FCSTD DOCUMENT  (FreeCAD 0.19R21897 (Git))
Label: MASTER2
License: cc-by-sa
LicenseURL: http://creativecommons.org/licenses/by-sa/4.0/
objects: Sketcher::SketchObject×2, PartDesign::Line×1, PartDesign::Plane×1, PartDesign::Body×1
note: 5 computed .brp shape members not serialized (recipe doc carries the construction recipe); baked Part::Feature solids carry a one-line shape summary decoded from their .brp

FEATURE [Sketcher::SketchObject] Sketch  label="MASTER"
  MapMode = 5
  Placement = pos=(0,0,0) rot=(0.57735,0.57735,0.57735;2.0944rad)
  Support = -> [YZ_Plane]
  sketch-geometry (3):
    g0: Circle CenterX=0 CenterY=1066.8 CenterZ=0 NormalX=0 NormalY=0 NormalZ=1 AngleXU=0 Radius=10
    g1: LineSegment StartX=-609.6 StartY=0 StartZ=0 EndX=304.8 EndY=0 EndZ=0
    g2: LineSegment StartX=0 StartY=1066.8 StartZ=0 EndX=0 EndY=0 EndZ=0
  constraints (9):
    c: PointOnObject(g1,g-1)
    c: PointOnObject(g1,g-1)
    c: Coincident(g2,g0)
    c: Vertical(g2)
    c: DistanceY(g0) = 1066.8
    c: DistanceX(g1,g1) = 914.4
    c: Coincident(g2,g-1)
    c: DistanceX(g2,g1) = 304.8
    c: Radius(g0) = 10
FEATURE [PartDesign::Line] DatumLine  label="RollerAxis"
  AttacherType = Attacher::AttachEngineLine
  Length = 20
  MapMode = 19
  Placement = pos=(-2.369e-13,2.363e-13,1066.8) rot=(0.57735,0.57735,0.57735;2.0944rad)
  ResizeMode = 0
  Support = -> [Sketch]
FEATURE [PartDesign::Plane] DatumPlane  label="HorizontalPlane"
  Length = 355.483
  MapMode = 49
  Placement = pos=(6.77e-14,304.8,-6.77e-14) rot=(0,0,-1;1.5708rad)
  ResizeMode = 0
  Support = -> [Sketch]
  Width = 75.6827
FEATURE [Sketcher::SketchObject] Sketch001  label="HorizontalMaster"
  ExternalGeometry = -> [Sketch]
  MapMode = 5
  Placement = pos=(6.77e-14,304.8,-6.77e-14) rot=(0,0,-1;1.5708rad)
  Support = -> [DatumPlane]
  sketch-geometry (4):
    g0: LineSegment StartX=304.8 StartY=1079.5 StartZ=0 EndX=304.8 EndY=-1079.5 EndZ=0
    g1: LineSegment StartX=0 StartY=1079.5 StartZ=0 EndX=914.4 EndY=1079.5 EndZ=0
    g2: LineSegment StartX=0 StartY=-1079.5 StartZ=0 EndX=914.4 EndY=-1079.5 EndZ=0
    g3: LineSegment [constr] StartX=0 StartY=1079.5 StartZ=0 EndX=0 EndY=-1079.5 EndZ=0
  constraints (13):
    c: Symmetric(g0,g0,g-1)
    c: PointOnObject(g-4,g0)
    c: DistanceY(g0,g0) = 2159
    c: Horizontal(g1)
    c: Horizontal(g2)
    c: PointOnObject(g0,g2)
    c: Equal(g1,g2)
    c: Coincident(g3,g1)
    c: Coincident(g3,g2)
    c: Vertical(g3)
    c: PointOnObject(g-1,g3)
    c: Equal(g2,g-3)
    c: PointOnObject(g0,g1)
FEATURE [PartDesign::Body] Body  label="Master"
  Group = -> [Sketch,DatumLine,DatumPlane,Sketch001]
  Origin = -> Origin
